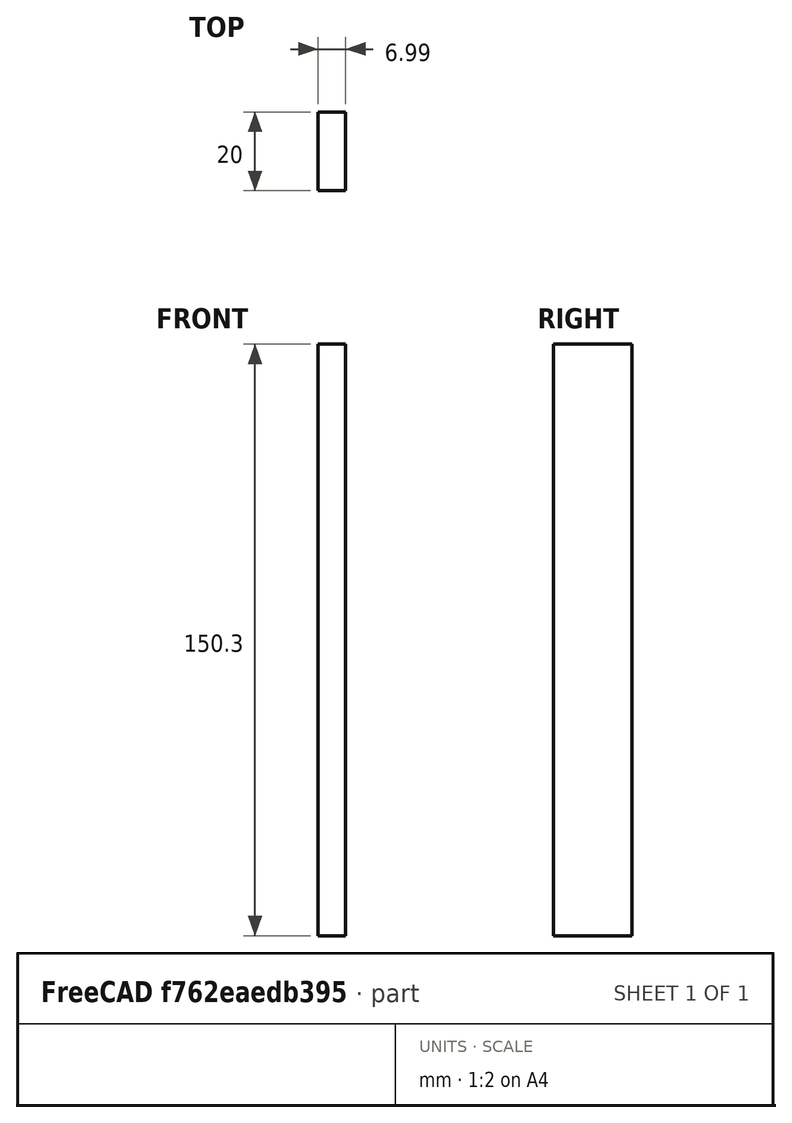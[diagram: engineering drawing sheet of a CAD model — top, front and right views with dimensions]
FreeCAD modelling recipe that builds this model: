
FCSTD DOCUMENT  (FreeCAD 0.18R4 (GitTag))
Label: bottle
License: All rights reserved
LicenseURL: http://en.wikipedia.org/wiki/All_rights_reserved
objects: Sketcher::SketchObject×5, Part::Revolution×3, Part::Extrusion×1
note: 9 computed .brp shape members not serialized (recipe doc carries the construction recipe); baked Part::Feature solids carry a one-line shape summary decoded from their .brp

FEATURE [Sketcher::SketchObject] Sketch
  Placement = pos=(0,0,0) rot=(1,0,0;1.5708rad)
  sketch-geometry (20):
    g0: LineSegment StartX=-5 StartY=60 StartZ=0 EndX=0 EndY=60 EndZ=0
    g1: ArcOfCircle CenterX=-18.369 CenterY=48.4328 CenterZ=0 NormalX=0 NormalY=0 NormalZ=1 AngleXU=0 Radius=1.66879 StartAngle=1.41669 EndAngle=2.99421
    g2: ArcOfCircle CenterX=-24.404 CenterY=29.1039 CenterZ=0 NormalX=0 NormalY=0 NormalZ=1 AngleXU=0 Radius=11.7525 StartAngle=0.631017 EndAngle=1.18669
    g3: ArcOfCircle CenterX=-14.5267 CenterY=34.9126 CenterZ=0 NormalX=0 NormalY=0 NormalZ=1 AngleXU=0 Radius=1.18984 StartAngle=1.90298 EndAngle=4.25339
    g4: ArcOfCircle CenterX=-14.383 CenterY=32.6458 CenterZ=0 NormalX=0 NormalY=0 NormalZ=1 AngleXU=0 Radius=1.3749 StartAngle=2.08053 EndAngle=4.26913
    g5: ArcOfCircle CenterX=-14.4564 CenterY=30.2525 CenterZ=0 NormalX=0 NormalY=0 NormalZ=1 AngleXU=0 Radius=1.26173 StartAngle=1.99232 EndAngle=4.29519
    g6: ArcOfCircle CenterX=-20.8451 CenterY=31.1761 CenterZ=0 NormalX=0 NormalY=0 NormalZ=1 AngleXU=0 Radius=6.23363 StartAngle=4.84838 EndAngle=5.94349
    g7: ArcOfCircle CenterX=-15.4255 CenterY=4.42693 CenterZ=0 NormalX=0 NormalY=0 NormalZ=1 AngleXU=0 Radius=4.57481 StartAngle=3.19068 EndAngle=4.47321
    g8: LineSegment StartX=0 StartY=0 StartZ=0 EndX=-16.5093 EndY=-0.017654 EndZ=0
    g9: LineSegment StartX=-19.9948 StartY=4.20248 StartZ=0 EndX=-20 EndY=25 EndZ=0
    g10: LineSegment StartX=-20 StartY=40 StartZ=0 EndX=-20.067 EndY=48.6094 EndZ=0
    g11: ArcOfCircle CenterX=-19.4495 CenterY=73.5852 CenterZ=0 NormalX=0 NormalY=0 NormalZ=1 AngleXU=0 Radius=23.5414 StartAngle=4.7692 EndAngle=5.37324
    g12: LineSegment StartX=-5 StartY=55 StartZ=0 EndX=-4.99946 EndY=57.4971 EndZ=0
    g13: LineSegment StartX=-4.96803 StartY=57.5285 StartZ=0 EndX=-4.20319 EndY=57.9057 EndZ=0
    g14: LineSegment StartX=-4.20319 StartY=57.9057 StartZ=0 EndX=-4.98898 EndY=58.3667 EndZ=0
    g15: LineSegment StartX=-4.97851 StartY=58.3877 StartZ=0 EndX=-4.23463 EndY=58.7125 EndZ=0
    g16: LineSegment StartX=-4.23463 StartY=58.7125 StartZ=0 EndX=-4.97851 EndY=59.1106 EndZ=0
    g17: LineSegment StartX=-4.94707 StartY=59.142 StartZ=0 EndX=-4.27653 EndY=59.5506 EndZ=0
    g18: LineSegment StartX=-4.2451 StartY=59.5716 StartZ=0 EndX=-5 EndY=60 EndZ=0
    g19: LineSegment StartX=0 StartY=60 StartZ=0 EndX=0 EndY=0 EndZ=0
FEATURE [Part::Revolution] Revolve
  Angle = 360
  Axis = (0,0,1)
  Base = (0,0,0)
  FaceMakerClass = Part::FaceMakerBullseye
  Solid = false
  Source = -> Sketch
  Symmetric = false
FEATURE [Sketcher::SketchObject] Sketch001
  Placement = pos=(0,0,0) rot=(1,0,0;1.5708rad)
  sketch-geometry (6):
    g0: LineSegment StartX=-8.24222 StartY=57.4492 StartZ=0 EndX=-8.20744 EndY=61.1712 EndZ=0
    g1: LineSegment StartX=-8.24093 StartY=57.4427 StartZ=0 EndX=-5.5213 EndY=57.4427 EndZ=0
    g2: LineSegment StartX=-5.5213 StartY=57.4427 StartZ=0 EndX=-5.5213 EndY=60.2248 EndZ=0
    g3: LineSegment StartX=-5.5213 StartY=60.2248 StartZ=0 EndX=0.011748 EndY=60.2248 EndZ=0
    g4: LineSegment StartX=0.011748 StartY=60.2248 StartZ=0 EndX=0.012077 EndY=61.2708 EndZ=0
    g5: LineSegment StartX=0.014913 StartY=61.2708 StartZ=0 EndX=-8.20654 EndY=61.1735 EndZ=0
FEATURE [Part::Revolution] Revolve001
  Angle = 360
  Axis = (0,0,1)
  Base = (0,0,0)
  FaceMakerClass = Part::FaceMakerBullseye
  Solid = false
  Source = -> Sketch001
  Symmetric = false
FEATURE [Sketcher::SketchObject] Sketch002
  Placement = pos=(0,0,0) rot=(1,0,0;1.5708rad)
  sketch-geometry (4):
    g0: LineSegment StartX=-16.2219 StartY=36.1575 StartZ=0 EndX=-21.7226 EndY=36.1575 EndZ=0
    g1: LineSegment StartX=-21.7226 StartY=36.1575 StartZ=0 EndX=-21.7226 EndY=28.7886 EndZ=0
    g2: LineSegment StartX=-21.7226 StartY=28.7886 StartZ=0 EndX=-16.2219 EndY=28.7886 EndZ=0
    g3: LineSegment StartX=-16.2219 StartY=28.7886 StartZ=0 EndX=-16.2219 EndY=36.1575 EndZ=0
  constraints (8):
    c: Coincident(g0,g1)
    c: Coincident(g1,g2)
    c: Coincident(g2,g3)
    c: Coincident(g3,g0)
    c: Horizontal(g0)
    c: Horizontal(g2)
    c: Vertical(g1)
    c: Vertical(g3)
FEATURE [Sketcher::SketchObject] Sketch003
  Placement = pos=(0,0,0) rot=(1,0,0;1.5708rad)
  sketch-geometry (7):
    g0: LineSegment StartX=21.2935 StartY=-0.740814 StartZ=0 EndX=21.2935 EndY=6.53631 EndZ=0
    g1: LineSegment StartX=21.4483 StartY=6.30406 StartZ=0 EndX=26.0933 EndY=6.30406 EndZ=0
    g2: LineSegment StartX=26.0933 StartY=6.30406 StartZ=0 EndX=26.0933 EndY=-4.45679 EndZ=0
    g3: LineSegment StartX=26.0933 StartY=-4.45679 StartZ=0 EndX=0.158835 EndY=-4.53421 EndZ=0
    g4: LineSegment StartX=0.158835 StartY=-4.53421 StartZ=0 EndX=0.236256 EndY=-0.895646 EndZ=0
    g5: LineSegment StartX=0.236256 StartY=-0.895646 StartZ=0 EndX=21.2161 EndY=-0.818229 EndZ=0
    g6: LineSegment StartX=21.2161 StartY=-0.818229 StartZ=0 EndX=21.294 EndY=-0.741304 EndZ=0
FEATURE [Part::Revolution] Revolve002
  Angle = 360
  Axis = (0,0,1)
  Base = (0,0,0)
  FaceMakerClass = Part::FaceMakerBullseye
  Placement = pos=(0,0,-90) rot=(0,0,1;0rad)
  Solid = false
  Source = -> Sketch003
  Symmetric = false
FEATURE [Sketcher::SketchObject] Sketch004
  Placement = pos=(0,0,0) rot=(1,0,0;1.5708rad)
  sketch-geometry (4):
    g0: LineSegment StartX=-23.4737 StartY=-6.04122 StartZ=0 EndX=-30.4601 EndY=-6.04122 EndZ=0
    g1: LineSegment StartX=-30.4601 StartY=-6.04122 StartZ=0 EndX=-30.4601 EndY=144.256 EndZ=0
    g2: LineSegment StartX=-30.4601 StartY=144.256 StartZ=0 EndX=-23.4737 EndY=144.256 EndZ=0
    g3: LineSegment StartX=-23.4737 StartY=144.256 StartZ=0 EndX=-23.4737 EndY=-6.04122 EndZ=0
  constraints (8):
    c: Coincident(g0,g1)
    c: Coincident(g1,g2)
    c: Coincident(g2,g3)
    c: Coincident(g3,g0)
    c: Horizontal(g0)
    c: Horizontal(g2)
    c: Vertical(g1)
    c: Vertical(g3)
FEATURE [Part::Extrusion] Extrude
  Base = -> Sketch004
  Dir = (0,-1,2e-16)
  DirMode = 2
  FaceMakerClass = Part::FaceMakerBullseye
  LengthFwd = 20
  LengthRev = 0
  Placement = pos=(0,0,-90) rot=(0,0,1;0rad)
  Solid = true
  Symmetric = true
